# Revit family: CLVRBRT-CF-WP
name_source: partatom
category: Lighting Devices
units: mm (PartAtom-declared; Revit-internal decimal feet)

## family parameters
Cut with Voids When Loaded = No
Host = Face
Maintain Annotation Orientation = No
Part Type = Normal
Room Calculation Point = No
Round Connector Dimension = Use Diameter
Shared = No

## types (1)
- CLVRBRT-CF-WP
    Clevertronics_Annotation Size = 0 mm  [stored 0 ft]
    Clevertronics_Construction = Powder Coated Steel
    Clevertronics_Dimensions Main Enclosure = L400mm x W150mm x H60mm
    Clevertronics_Height = 60 mm
    Clevertronics_Length = 400 mm
    Clevertronics_Material = Clevertronics_Metal, Powder Coated, White
    Clevertronics_Mounting = Surface Wall Mounted
    Clevertronics_Product Description = Cantilever Bracket for Cleverfit and Universal Weatherproof Exit, White,including all Fixings needed to fix the Product to the Bracket.
    Clevertronics_Suitable Fittings = Cleverfit Exit: ECFLED, CCFLED, LCFLED // Universal Weatherproof Exit: EWELED, CWELED, LWELED, LCWELED
    Clevertronics_Weight = 1.5 Kg
    Clevertronics_Width = 150 mm
    Default Elevation = 1200 mm
    Description = Cantilever Bracket for Cleverfit and Universal Weatherproof Exit, White,including all Fixings needed to fix the Product to the Bracket.
    Manufacturer = Clevertronics
    Model = CLVRBRT-CF-WP

note: [stored X ft] marks values corroborated as IEEE doubles in the binary element streams (Revit-internal decimal feet)

## geometry (parser evidence)
native form markers: Blend x2, Sweep x3
no freeform markers — native parametric forms only
